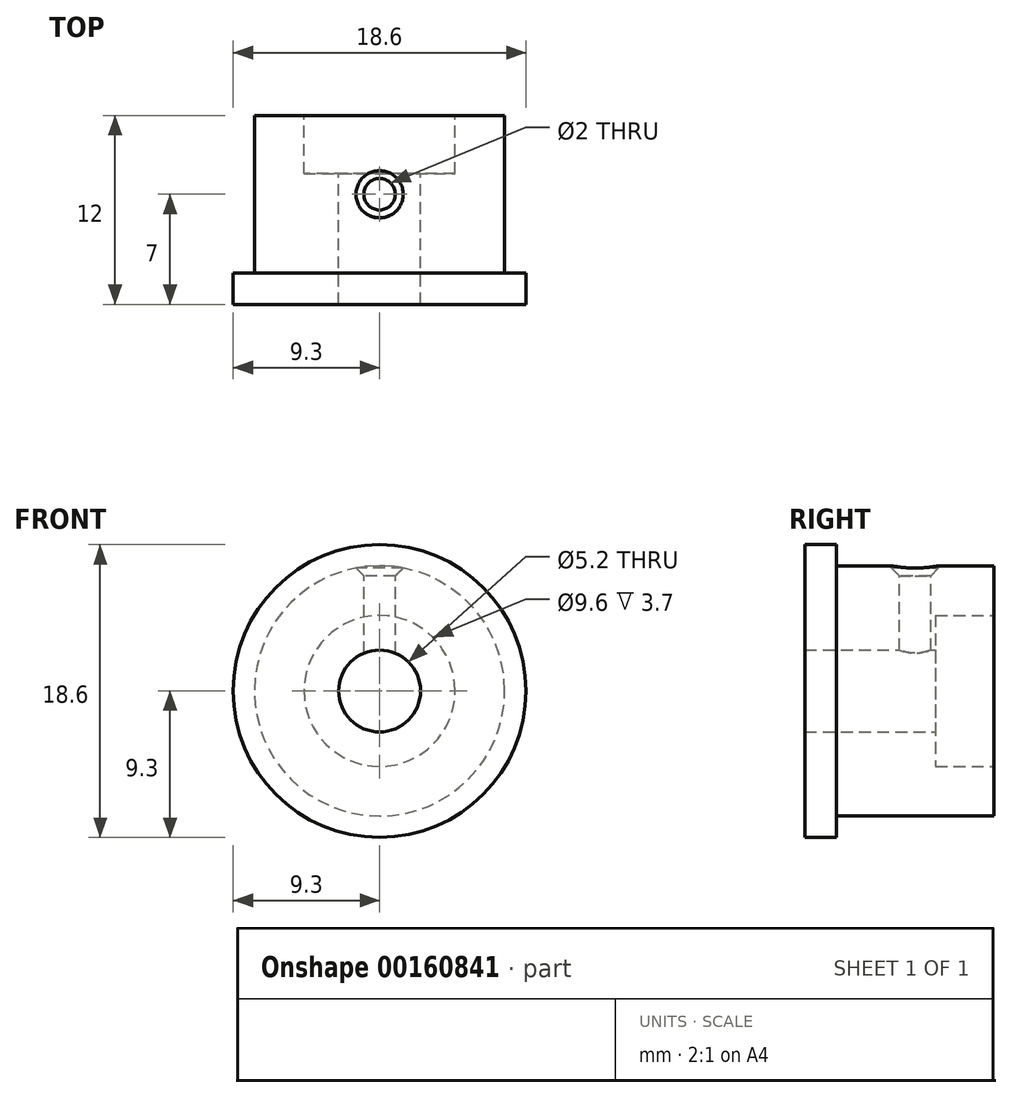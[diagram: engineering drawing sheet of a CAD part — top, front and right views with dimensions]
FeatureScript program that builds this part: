
annotation { "Feature Type Name" : "Feature", "Feature Type Description" : "" }
export const myFeature = defineFeature(function(context is Context, id is Id, definition is map)
    precondition{}
    {
        {
            assignVariable(context, id + "F0", {"name" : "OutDiam_Relief", "anyValue" : 15.9});
        }
        {
            assignVariable(context, id + "F1", {"name" : "InDiam_Bore", "anyValue" : 2});
        }
        {
            var Q0;
            Q0=qCreatedBy(makeId("Right.planeOp"),FACE);
            var sketch = newSketch(context, id + "F2", { "sketchPlane" : qUnion([Q0])});
            skLineSegment(sketch, "E0", {"start": v(11.47, 0) * mm, "end": v(0, 0) * mm, "construction": true});
            skLineSegment(sketch, "E1", {"start": v(8.3, 2.6) * mm, "end": v(0, 2.6) * mm});
            skLineSegment(sketch, "E2", {"start": v(8.3, 2.6) * mm, "end": v(8.3, 4.8) * mm});
            skLineSegment(sketch, "E3", {"start": v(12, 4.8) * mm, "end": v(8.3, 4.8) * mm});
            skLineSegment(sketch, "E4", {"start": v(12, 4.8) * mm, "end": v(12, 7.95) * mm});
            skLineSegment(sketch, "E5", {"start": v(2, 7.95) * mm, "end": v(12, 7.95) * mm});
            skLineSegment(sketch, "E6", {"start": v(2, 7.95) * mm, "end": v(2, 9.3) * mm});
            skLineSegment(sketch, "E7", {"start": v(0, 9.3) * mm, "end": v(2, 9.3) * mm});
            skLineSegment(sketch, "E8", {"start": v(0, 9.3) * mm, "end": v(0, 2.6) * mm});
            skSolve(sketch);
        }
        {
            var Q0;
            Q0=makeQuery(id+"F2.imprint","IMPRINT",FACE,{"disambiguationData":[TD([[makeQuery(id+"F2.imprint","IMPRINT",EDGE,{"derivedFrom":sQuery(id+"F2.wireOp",EDGE,"E1")}),-1.0]])]});
            var Q1;
            Q1=sQuery(id+"F2.wireOp",EDGE,"E0");
            revolve(context, id + "F3", {"entities" : qUnion([Q0]), "axis" : qUnion([Q1]), "revolveType" : RevolveType.FULL});
        }
        {
            var Q0;
            Q0=qCreatedBy(makeId("Top.planeOp"),FACE);
            cPlane(context, id + "F4", {"entities" : qUnion([Q0]), "cplaneType" : CPlaneType.OFFSET, "offset" : (getVariable(context, 'OutDiam_Relief')) * mm / 2, "width" : 150 * mm, "height" : 150 * mm});
        }
        {
            var Q0;
            Q0=qCreatedBy(id+"F4.planeOp",FACE);
            var sketch = newSketch(context, id + "F5", { "sketchPlane" : qUnion([Q0])});
            skCircle(sketch, "E9", {"center": v(0, 7) * mm, "radius": 1 * mm});
            skLineSegment(sketch, "E10.0", {"start": v(-7.95, 12) * mm, "end": v(7.95, 12) * mm});
            skSolve(sketch);
        }
        {
            var Q0;
            Q0=sQuery(id+"F5.wireOp",VERTEX,"E9.center");
            var Q1;
            Q1=makeQuery(id+"F3.opRevolve","SWEPT_BODY",BODY,{"disambiguationData":[OSD([sQuery(id+"F2.wireOp",EDGE,"E1"),sQuery(id+"F2.wireOp",EDGE,"E2"),sQuery(id+"F2.wireOp",EDGE,"E3"),sQuery(id+"F2.wireOp",EDGE,"E4"),sQuery(id+"F2.wireOp",EDGE,"E5"),sQuery(id+"F2.wireOp",EDGE,"E6"),sQuery(id+"F2.wireOp",EDGE,"E7"),sQuery(id+"F2.wireOp",EDGE,"E8")])]});
            hole(context, id + "F6", {"style" : HoleStyle.C_SINK, "endStyle" : HoleEndStyle.BLIND, "holeDiameter" : (getVariable(context, 'InDiam_Bore')) * mm, "cSinkDiameter" : 3 * mm, "cSinkAngle" : 90 * degree, "holeDepth" : 8 * mm, "locations" : qUnion([Q0]), "scope" : qUnion([Q1])});
        }
    });
